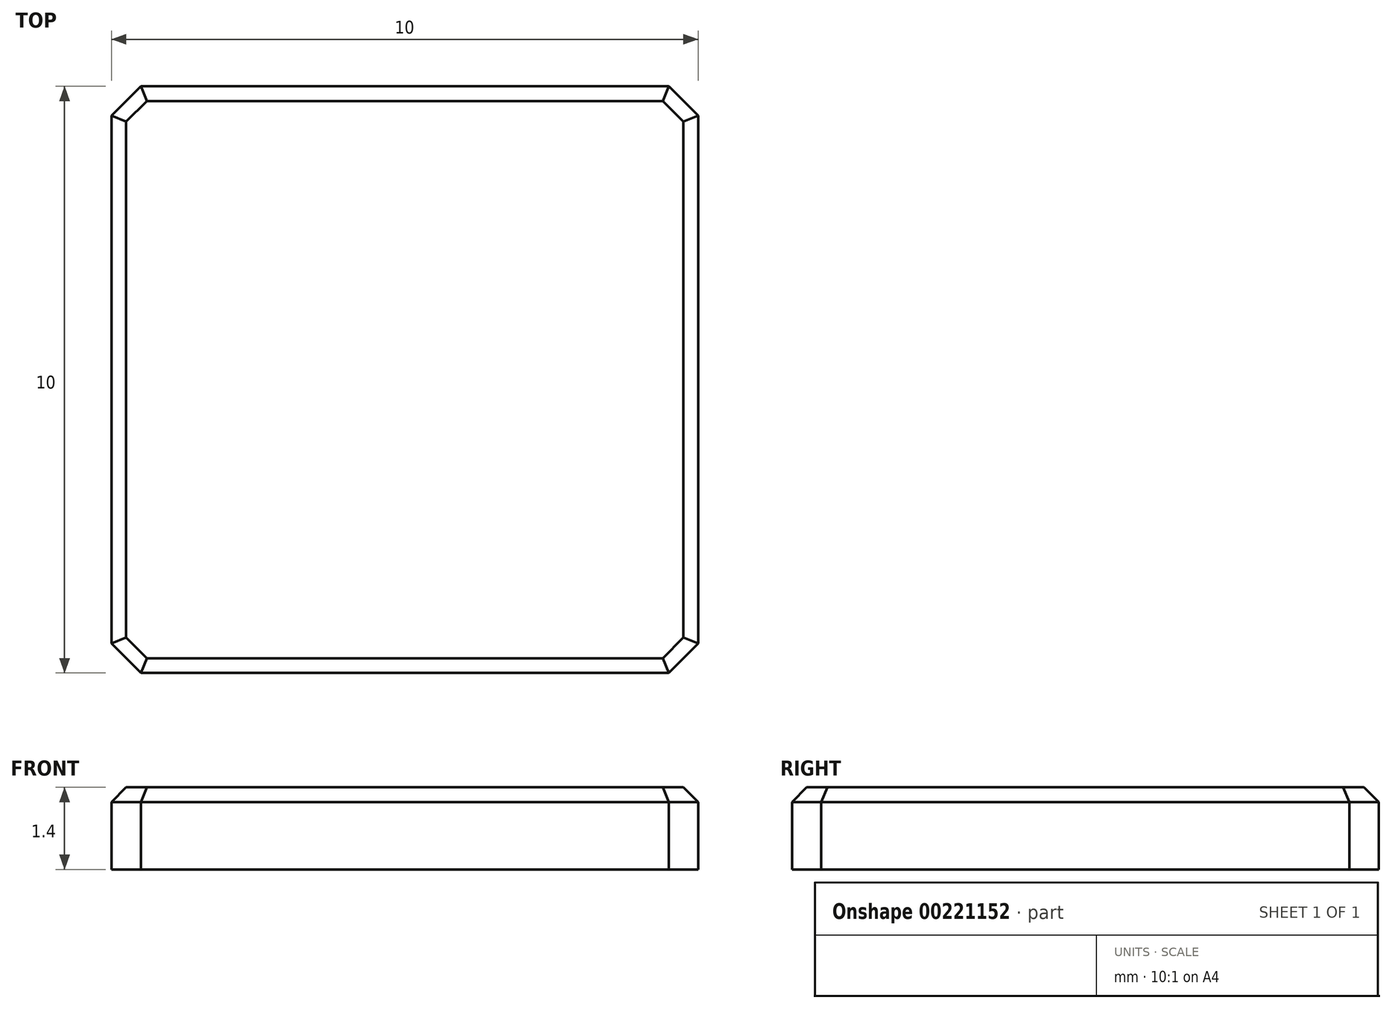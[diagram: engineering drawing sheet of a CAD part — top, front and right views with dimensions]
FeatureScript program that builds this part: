
annotation { "Feature Type Name" : "Feature", "Feature Type Description" : "" }
export const myFeature = defineFeature(function(context is Context, id is Id, definition is map)
    precondition{}
    {
        {
            var Q0;
            Q0=qCreatedBy(makeId("Top.planeOp"),FACE);
            var sketch = newSketch(context, id + "F0", { "sketchPlane" : qUnion([Q0])});
            skLineSegment(sketch, "E0", {"start": v(0, 0) * mm, "end": v(0, 5) * mm, "construction": true});
            skLineSegment(sketch, "E1", {"start": v(0, 0) * mm, "end": v(0, -5) * mm, "construction": true});
            skLineSegment(sketch, "E2", {"start": v(0, 0) * mm, "end": v(-5, 0) * mm, "construction": true});
            skLineSegment(sketch, "E3", {"start": v(0, 0) * mm, "end": v(5, 0) * mm, "construction": true});
            skLineSegment(sketch, "E4", {"start": v(5, -5) * mm, "end": v(5, 5) * mm});
            skLineSegment(sketch, "E5", {"start": v(-5, 5) * mm, "end": v(5, 5) * mm});
            skLineSegment(sketch, "E6", {"start": v(-5, 5) * mm, "end": v(-5, -5) * mm});
            skLineSegment(sketch, "E7", {"start": v(-5, -5) * mm, "end": v(5, -5) * mm});
            skSolve(sketch);
        }
        {
            var Q0;
            Q0 = qSketchRegion(id + "F0", true);
            extrude(context, id + "F1", {"entities" : qUnion([Q0]), "depth" : 1.4 * mm});
        }
        {
            var Q0;
            Q0=makeQuery(id+"F1.opExtrude","SWEPT_EDGE",EDGE,{"disambiguationData":[OSD([sQuery(id+"F0.wireOp",EDGE,"E4"),sQuery(id+"F0.wireOp",EDGE,"E5")])]});
            var Q1;
            Q1=makeQuery(id+"F1.opExtrude","SWEPT_EDGE",EDGE,{"disambiguationData":[OSD([sQuery(id+"F0.wireOp",EDGE,"E5"),sQuery(id+"F0.wireOp",EDGE,"E6")])]});
            var Q2;
            Q2=makeQuery(id+"F1.opExtrude","SWEPT_EDGE",EDGE,{"disambiguationData":[OSD([sQuery(id+"F0.wireOp",EDGE,"E4"),sQuery(id+"F0.wireOp",EDGE,"E7")])]});
            var Q3;
            Q3=makeQuery(id+"F1.opExtrude","SWEPT_EDGE",EDGE,{"disambiguationData":[OSD([sQuery(id+"F0.wireOp",EDGE,"E6"),sQuery(id+"F0.wireOp",EDGE,"E7")])]});
            chamfer(context, id + "F2", {"entities" : qUnion([Q0, Q1, Q2, Q3]), "width" : .5 * mm, "tangentPropagation" : true});
        }
        {
            var Q0;
            Q0=makeQuery(id+"F1.opExtrude","CAP_EDGE",EDGE,{"disambiguationData":[OSD([sQuery(id+"F0.wireOp",EDGE,"E5")])],"isStart":false});
            var Q1;
            Q1=makeQuery(id+"F1.opExtrude","CAP_EDGE",EDGE,{"disambiguationData":[OSD([sQuery(id+"F0.wireOp",EDGE,"E6")])],"isStart":false});
            var Q2;
            {var subQ0=sQuery(id+"F0.wireOp",EDGE,"E6");var subQ1=sQuery(id+"F0.wireOp",EDGE,"E5");Q2=makeQuery(id+"F2.opChamfer","BLEND_EDGE",EDGE,{"blendedFrom":[makeQuery(id+"F1.opExtrude","SWEPT_EDGE",EDGE,{"disambiguationData":[OSD([subQ1,subQ0])]}),makeQuery(id+"F1.opExtrude","CAP_FACE",FACE,{"disambiguationData":[OSD([sQuery(id+"F0.wireOp",EDGE,"E4"),subQ1,subQ0,sQuery(id+"F0.wireOp",EDGE,"E7")])],"isStart":false})],"blendedInto":[makeQuery(id+"F1.opExtrude","CAP_FACE",FACE,{"disambiguationData":[OSD([sQuery(id+"F0.wireOp",EDGE,"E4"),subQ1,subQ0,sQuery(id+"F0.wireOp",EDGE,"E7")])],"isStart":false})]});}
            var Q3;
            Q3=makeQuery(id+"F1.opExtrude","CAP_EDGE",EDGE,{"disambiguationData":[OSD([sQuery(id+"F0.wireOp",EDGE,"E7")])],"isStart":false});
            var Q4;
            {var subQ0=sQuery(id+"F0.wireOp",EDGE,"E7");var subQ1=sQuery(id+"F0.wireOp",EDGE,"E6");Q4=makeQuery(id+"F2.opChamfer","BLEND_EDGE",EDGE,{"blendedFrom":[makeQuery(id+"F1.opExtrude","SWEPT_EDGE",EDGE,{"disambiguationData":[OSD([subQ1,subQ0])]}),makeQuery(id+"F1.opExtrude","CAP_FACE",FACE,{"disambiguationData":[OSD([sQuery(id+"F0.wireOp",EDGE,"E4"),sQuery(id+"F0.wireOp",EDGE,"E5"),subQ1,subQ0])],"isStart":false})],"blendedInto":[makeQuery(id+"F1.opExtrude","CAP_FACE",FACE,{"disambiguationData":[OSD([sQuery(id+"F0.wireOp",EDGE,"E4"),sQuery(id+"F0.wireOp",EDGE,"E5"),subQ1,subQ0])],"isStart":false})]});}
            var Q5;
            {var subQ0=sQuery(id+"F0.wireOp",EDGE,"E7");var subQ1=sQuery(id+"F0.wireOp",EDGE,"E4");Q5=makeQuery(id+"F2.opChamfer","BLEND_EDGE",EDGE,{"blendedFrom":[makeQuery(id+"F1.opExtrude","SWEPT_EDGE",EDGE,{"disambiguationData":[OSD([subQ1,subQ0])]}),makeQuery(id+"F1.opExtrude","CAP_FACE",FACE,{"disambiguationData":[OSD([subQ1,sQuery(id+"F0.wireOp",EDGE,"E5"),sQuery(id+"F0.wireOp",EDGE,"E6"),subQ0])],"isStart":false})],"blendedInto":[makeQuery(id+"F1.opExtrude","CAP_FACE",FACE,{"disambiguationData":[OSD([subQ1,sQuery(id+"F0.wireOp",EDGE,"E5"),sQuery(id+"F0.wireOp",EDGE,"E6"),subQ0])],"isStart":false})]});}
            var Q6;
            Q6=makeQuery(id+"F1.opExtrude","CAP_EDGE",EDGE,{"disambiguationData":[OSD([sQuery(id+"F0.wireOp",EDGE,"E4")])],"isStart":false});
            var Q7;
            {var subQ0=sQuery(id+"F0.wireOp",EDGE,"E5");var subQ1=sQuery(id+"F0.wireOp",EDGE,"E4");Q7=makeQuery(id+"F2.opChamfer","BLEND_EDGE",EDGE,{"blendedFrom":[makeQuery(id+"F1.opExtrude","SWEPT_EDGE",EDGE,{"disambiguationData":[OSD([subQ1,subQ0])]}),makeQuery(id+"F1.opExtrude","CAP_FACE",FACE,{"disambiguationData":[OSD([subQ1,subQ0,sQuery(id+"F0.wireOp",EDGE,"E6"),sQuery(id+"F0.wireOp",EDGE,"E7")])],"isStart":false})],"blendedInto":[makeQuery(id+"F1.opExtrude","CAP_FACE",FACE,{"disambiguationData":[OSD([subQ1,subQ0,sQuery(id+"F0.wireOp",EDGE,"E6"),sQuery(id+"F0.wireOp",EDGE,"E7")])],"isStart":false})]});}
            chamfer(context, id + "F3", {"entities" : qUnion([Q0, Q1, Q2, Q3, Q4, Q5, Q6, Q7]), "width" : .25 * mm, "tangentPropagation" : true});
        }
    });
